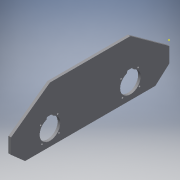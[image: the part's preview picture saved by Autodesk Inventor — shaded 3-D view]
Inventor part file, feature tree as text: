
AUTODESK INVENTOR PART (.ipt)
format: ipt  version: 2019 (Build 230136000, 136)  size: 387,072 bytes
history: native  units: mm
features: reference x20, other x6, sketch x3, extrude x2
ambient origin geometry x8: Origin, YZ Plane, XZ Plane, XY Plane, X Axis, Y Axis, Z Axis, Center Point
bodies: Body1 (feature_tree)
feature tree (31):
  other  "Твердое тело1"
  extrude  "Выдавливание1"  Depth=67.0mm
  sketch  "Эскиз2"
  extrude  "Выдавливание2"  Depth=50.0mm
  sketch  "Эскиз1"
  reference  "Ссылка1"
  reference  "Ссылка2"
  reference  "Ссылка3"
  reference  "Ссылка4"
  reference  "Ссылка5"
  reference  "Ссылка6"
  reference  "Ссылка7"
  reference  "Ссылка8"
  reference  "Ссылка9"
  reference  "Ссылка10"
  reference  "Ссылка11"
  reference  "Ссылка12"
  reference  "Ссылка13"
  reference  "Ссылка14"
  reference  "Ссылка15"
  reference  "Ссылка16"
  reference  "Ссылка17"
  reference  "Ссылка18"
  reference  "Ссылка19"
  reference  "Ссылка20"
  sketch  "Эскиз3"
  other  "Сборка2"
  other  "Моторный блок:1"
  other  "mot37:1"
  other  "Моторный блок:2"
  other  "Диск.0001:1"
